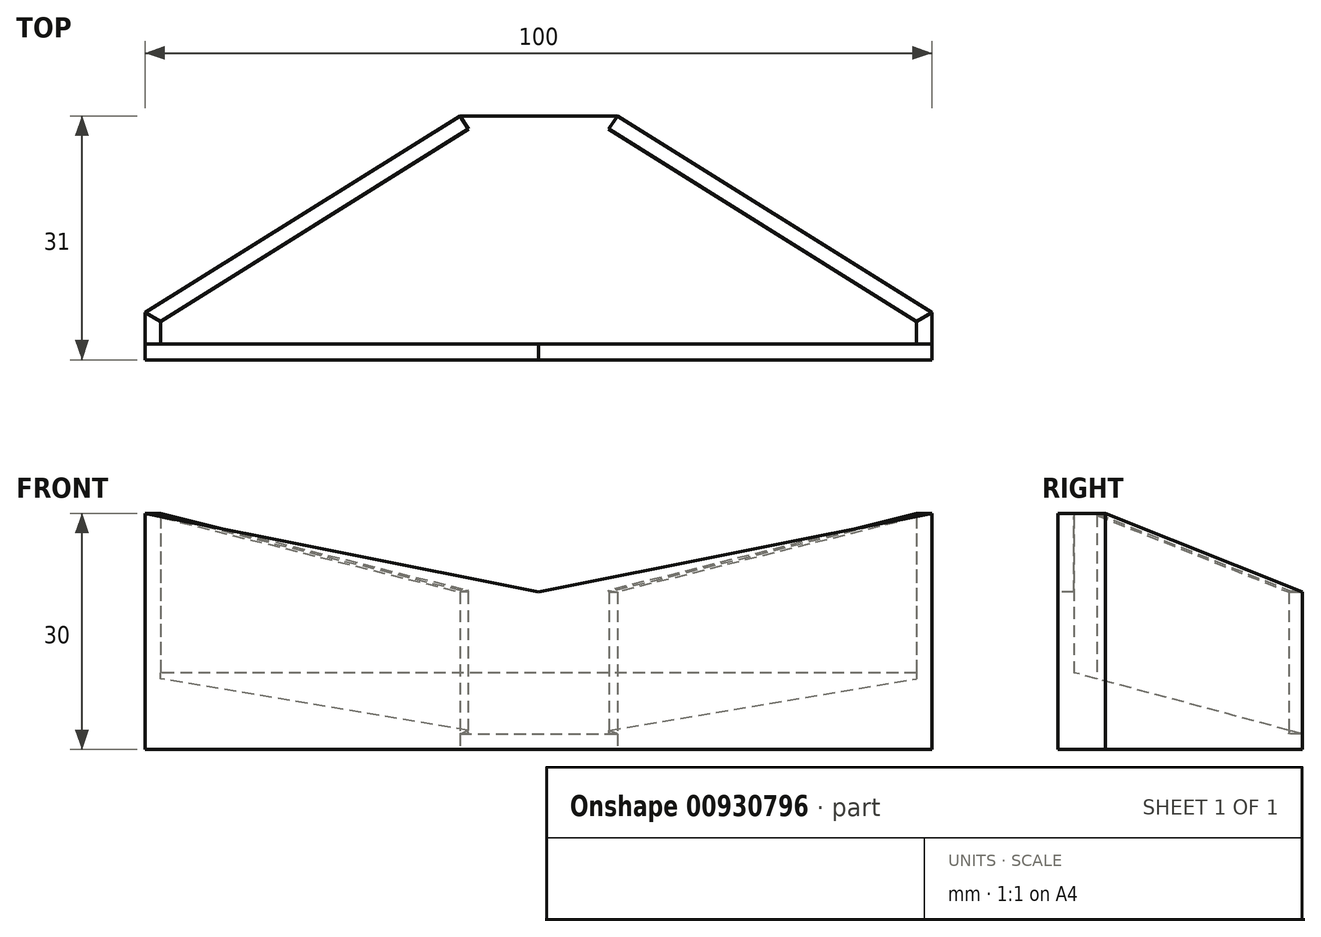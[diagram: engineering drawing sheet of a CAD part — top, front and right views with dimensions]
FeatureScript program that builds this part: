
annotation { "Feature Type Name" : "Feature", "Feature Type Description" : "" }
export const myFeature = defineFeature(function(context is Context, id is Id, definition is map)
    precondition{}
    {
        {
            var Q0;
            Q0=qCreatedBy(makeId("Top.planeOp"),FACE);
            var sketch = newSketch(context, id + "F0", { "sketchPlane" : qUnion([Q0])});
            skLineSegment(sketch, "E0", {"start": v(0, 0) * mm, "end": v(-50, 0) * mm});
            skLineSegment(sketch, "E1", {"start": v(-50, 0) * mm, "end": v(-50, 6) * mm});
            skLineSegment(sketch, "E2", {"start": v(-50, 6) * mm, "end": v(-10, 31) * mm});
            skLineSegment(sketch, "E3", {"start": v(-10, 31) * mm, "end": v(0, 31) * mm});
            skLineSegment(sketch, "E4.MirrorCS", {"start": v(50, 6) * mm, "end": v(10, 31) * mm});
            skLineSegment(sketch, "E5.MirrorCS", {"start": v(50, 0) * mm, "end": v(50, 6) * mm});
            skLineSegment(sketch, "E6.MirrorCS", {"start": v(10, 31) * mm, "end": v(0, 31) * mm});
            skLineSegment(sketch, "E7.MirrorCS", {"start": v(0, 0) * mm, "end": v(50, 0) * mm});
            skLineSegment(sketch, "E8.0", {"start": v(-48, 2) * mm, "end": v(-48, 4.9) * mm});
            skLineSegment(sketch, "E8.1", {"start": v(0, 2) * mm, "end": v(-48, 2) * mm});
            skLineSegment(sketch, "E8.2", {"start": v(-48, 4.9) * mm, "end": v(-9.43, 29) * mm});
            skLineSegment(sketch, "E8.3", {"start": v(0, 2) * mm, "end": v(48, 2) * mm});
            skLineSegment(sketch, "E8.6", {"start": v(48, 4.9) * mm, "end": v(9.43, 29) * mm});
            skLineSegment(sketch, "E8.7", {"start": v(48, 2) * mm, "end": v(48, 4.9) * mm});
            skLineSegment(sketch, "E9", {"start": v(-10, 31) * mm, "end": v(-9.43, 29) * mm});
            skLineSegment(sketch, "E10", {"start": v(10, 31) * mm, "end": v(9.43, 29) * mm});
            skLineSegment(sketch, "E11", {"start": v(-50, 6) * mm, "end": v(-48, 4.9) * mm});
            skLineSegment(sketch, "E12", {"start": v(48, 4.9) * mm, "end": v(50, 6) * mm});
            skSolve(sketch);
        }
        {
            var Q0;
            Q0=makeQuery(id+"F0.imprint","IMPRINT",FACE,{"disambiguationData":[TD([[makeQuery(id+"F0.imprint","IMPRINT",EDGE,{"derivedFrom":sQuery(id+"F0.wireOp",EDGE,"E0")}),-1.0]])]});
            var Q1;
            Q1 = qSketchRegion(id + "F4", true);
            extrude(context, id + "F1", {"entities" : qUnion([Q0, Q1]), "depth" : 30 * mm, "offsetDistance" : 25 * mm});
        }
        {
            var Q0;
            Q0=makeQuery(id+"F0.imprint","IMPRINT",FACE,{"disambiguationData":[TD([[makeQuery(id+"F0.imprint","IMPRINT",EDGE,{"derivedFrom":sQuery(id+"F0.wireOp",EDGE,"E3")}),-1.0]])]});
            extrude(context, id + "F2", {"entities" : qUnion([Q0]), "operationType" : NewBodyOperationType.ADD, "depth" : 2 * mm, "offsetDistance" : 25 * mm});
        }
        {
            var Q0;
            Q0=makeQuery(id+"F0.imprint","IMPRINT",FACE,{"disambiguationData":[TD([[makeQuery(id+"F0.imprint","IMPRINT",EDGE,{"derivedFrom":sQuery(id+"F0.wireOp",EDGE,"E2")}),-1.0]])]});
            var Q1;
            Q1=makeQuery(id+"F0.imprint","IMPRINT",FACE,{"disambiguationData":[TD([[makeQuery(id+"F0.imprint","IMPRINT",EDGE,{"derivedFrom":sQuery(id+"F0.wireOp",EDGE,"E4.MirrorCS")}),1.0]])]});
            extrude(context, id + "F3", {"entities" : qUnion([Q0, Q1]), "operationType" : NewBodyOperationType.ADD, "depth" : 20 * mm, "offsetDistance" : 25 * mm});
        }
        {
            var Q0;
            Q0=makeQuery(id+"F3.opExtrude","SWEPT_FACE",FACE,{"disambiguationData":[OSD([sQuery(id+"F0.wireOp",EDGE,"E2")])]});
            var sketch = newSketch(context, id + "F4", { "sketchPlane" : qUnion([Q0])});
            skLineSegment(sketch, "E13", {"start": v(-7.95, 20) * mm, "end": v(39.22, 20) * mm});
            skLineSegment(sketch, "E14", {"start": v(39.22, 20) * mm, "end": v(39.22, 30) * mm});
            skLineSegment(sketch, "E15", {"start": v(39.22, 30) * mm, "end": v(-7.95, 20) * mm});
            skSolve(sketch);
        }
        {
            var Q0;
            Q0=makeQuery(id+"F4.imprint","IMPRINT",FACE,{"disambiguationData":[TD([[makeQuery(id+"F4.imprint","IMPRINT",EDGE,{"derivedFrom":sQuery(id+"F4.wireOp",EDGE,"E13")}),-1.0]])]});
            extrude(context, id + "F5", {"entities" : qUnion([Q0]), "operationType" : NewBodyOperationType.ADD, "oppositeDirection" : true, "depth" : 2 * mm, "offsetDistance" : 25 * mm});
        }
        {
            var Q0;
            Q0=makeQuery(id+"F3.opExtrude","SWEPT_FACE",FACE,{"disambiguationData":[OSD([sQuery(id+"F0.wireOp",EDGE,"E4.MirrorCS")])]});
            var sketch = newSketch(context, id + "F6", { "sketchPlane" : qUnion([Q0])});
            skLineSegment(sketch, "E16", {"start": v(7.95, 20) * mm, "end": v(-39.22, 20) * mm});
            skLineSegment(sketch, "E17", {"start": v(-39.22, 20) * mm, "end": v(-39.22, 30) * mm});
            skLineSegment(sketch, "E18", {"start": v(-39.22, 30) * mm, "end": v(7.95, 20) * mm});
            skSolve(sketch);
        }
        {
            var Q0;
            Q0=makeQuery(id+"F6.imprint","IMPRINT",FACE,{"disambiguationData":[TD([[makeQuery(id+"F6.imprint","IMPRINT",EDGE,{"derivedFrom":sQuery(id+"F6.wireOp",EDGE,"E16")}),1.0]])]});
            extrude(context, id + "F7", {"entities" : qUnion([Q0]), "operationType" : NewBodyOperationType.ADD, "oppositeDirection" : true, "depth" : 2 * mm, "offsetDistance" : 25 * mm});
        }
        {
            var Q0;
            Q0=makeQuery(id+"F5.opExtrude","SWEPT_EDGE",EDGE,{"disambiguationData":[OSD([sQuery(id+"F0.wireOp",EDGE,"E2"),sQuery(id+"F0.wireOp",EDGE,"E3"),sQuery(id+"F0.wireOp",EDGE,"E9"),sQuery(id+"F4.wireOp",EDGE,"E13"),sQuery(id+"F4.wireOp",EDGE,"E15")])]});
            var Q1;
            Q1=makeQuery(id+"F3.boolean.opBoolean","SPLIT",EDGE,{"derivedFrom":makeQuery(id+"F3.opExtrude","SWEPT_EDGE",EDGE,{"disambiguationData":[OSD([sQuery(id+"F0.wireOp",EDGE,"E2"),sQuery(id+"F0.wireOp",EDGE,"E3"),sQuery(id+"F0.wireOp",EDGE,"E9")])]})});
            cPlane(context, id + "F8", {"entities" : qUnion([Q0, Q1]), "cplaneType" : CPlaneType.LINE_ANGLE, "offset" : 25 * mm, "angle" : 0 * degree, "width" : 150 * mm, "height" : 150 * mm});
        }
        {
            var Q0;
            Q0=qCreatedBy(id+"F8.planeOp",FACE);
            var sketch = newSketch(context, id + "F9", { "sketchPlane" : qUnion([Q0])});
            skLineSegment(sketch, "E19.bottom", {"start": v(-29.59, 20) * mm, "end": v(-31.59, 20) * mm});
            skLineSegment(sketch, "E19.top", {"start": v(-29.59, 2) * mm, "end": v(-31.59, 2) * mm});
            skLineSegment(sketch, "E19.left", {"start": v(-29.59, 20) * mm, "end": v(-29.59, 2) * mm});
            skLineSegment(sketch, "E19.right", {"start": v(-31.59, 20) * mm, "end": v(-31.59, 2) * mm});
            skSolve(sketch);
        }
        {
            var Q0;
            Q0=makeQuery(id+"F9.imprint","IMPRINT",FACE,{"disambiguationData":[TD([[makeQuery(id+"F9.imprint","IMPRINT",EDGE,{"derivedFrom":sQuery(id+"F9.wireOp",EDGE,"E19.bottom")}),1.0]])]});
            extrude(context, id + "F10", {"entities" : qUnion([Q0]), "operationType" : NewBodyOperationType.ADD, "depth" : 1 * mm, "offsetDistance" : 25 * mm});
        }
        {
            var Q0;
            Q0=makeQuery(id+"F7.opExtrude","SWEPT_EDGE",EDGE,{"disambiguationData":[OSD([sQuery(id+"F0.wireOp",EDGE,"E4.MirrorCS"),sQuery(id+"F0.wireOp",EDGE,"E6.MirrorCS"),sQuery(id+"F0.wireOp",EDGE,"E10"),sQuery(id+"F6.wireOp",EDGE,"E16"),sQuery(id+"F6.wireOp",EDGE,"E18")])]});
            var Q1;
            Q1=makeQuery(id+"F3.boolean.opBoolean","SPLIT",EDGE,{"derivedFrom":makeQuery(id+"F3.opExtrude","SWEPT_EDGE",EDGE,{"disambiguationData":[OSD([sQuery(id+"F0.wireOp",EDGE,"E4.MirrorCS"),sQuery(id+"F0.wireOp",EDGE,"E6.MirrorCS"),sQuery(id+"F0.wireOp",EDGE,"E10")])]})});
            cPlane(context, id + "F11", {"entities" : qUnion([Q0, Q1]), "cplaneType" : CPlaneType.LINE_ANGLE, "offset" : 25 * mm, "angle" : 0 * degree, "width" : 150 * mm, "height" : 150 * mm});
        }
        {
            var Q0;
            Q0=qCreatedBy(id+"F11.planeOp",FACE);
            var sketch = newSketch(context, id + "F12", { "sketchPlane" : qUnion([Q0])});
            skLineSegment(sketch, "E20.bottom", {"start": v(-31.59, 20) * mm, "end": v(-29.59, 20) * mm});
            skLineSegment(sketch, "E20.top", {"start": v(-31.59, 2) * mm, "end": v(-29.59, 2) * mm});
            skLineSegment(sketch, "E20.left", {"start": v(-31.59, 20) * mm, "end": v(-31.59, 2) * mm});
            skLineSegment(sketch, "E20.right", {"start": v(-29.59, 20) * mm, "end": v(-29.59, 2) * mm});
            skSolve(sketch);
        }
        {
            var Q0;
            Q0=makeQuery(id+"F12.imprint","IMPRINT",FACE,{"disambiguationData":[TD([[makeQuery(id+"F12.imprint","IMPRINT",EDGE,{"derivedFrom":sQuery(id+"F12.wireOp",EDGE,"E20.bottom")}),-1.0]])]});
            extrude(context, id + "F13", {"entities" : qUnion([Q0]), "operationType" : NewBodyOperationType.ADD, "oppositeDirection" : true, "depth" : 1 * mm, "offsetDistance" : 25 * mm});
        }
        {
            var Q0;
            Q0=makeQuery(id+"F5.opExtrude","CAP_EDGE",EDGE,{"disambiguationData":[OSD([sQuery(id+"F4.wireOp",EDGE,"E15")])],"isStart":true});
            var Q1;
            Q1=makeQuery(id+"F1.opExtrude","CAP_EDGE",EDGE,{"disambiguationData":[OSD([sQuery(id+"F0.wireOp",EDGE,"E11")])],"isStart":false});
            cPlane(context, id + "F14", {"entities" : qUnion([Q0, Q1]), "cplaneType" : CPlaneType.LINE_ANGLE, "offset" : 25 * mm, "angle" : 0 * degree, "width" : 150 * mm, "height" : 150 * mm});
        }
        {
            var Q0;
            Q0=qCreatedBy(id+"F14.planeOp",FACE);
            var sketch = newSketch(context, id + "F15", { "sketchPlane" : qUnion([Q0])});
            skLineSegment(sketch, "E21", {"start": v(-51.18, 1.42) * mm, "end": v(-11.81, -24.52) * mm});
            skLineSegment(sketch, "E22", {"start": v(-11.81, -24.52) * mm, "end": v(-12.9, -26.17) * mm});
            skLineSegment(sketch, "E23", {"start": v(-12.9, -26.17) * mm, "end": v(-53.17, 0.35) * mm});
            skLineSegment(sketch, "E24", {"start": v(-53.17, 0.35) * mm, "end": v(-51.18, 1.42) * mm});
            skSolve(sketch);
        }
        {
            var Q0;
            Q0=makeQuery(id+"F15.imprint","IMPRINT",FACE,{"disambiguationData":[TD([[makeQuery(id+"F15.imprint","IMPRINT",EDGE,{"derivedFrom":sQuery(id+"F15.wireOp",EDGE,"E21")}),-1.0]])]});
            var Q1;
            Q1=makeQuery(id+"F5.opExtrude","SWEPT_FACE",FACE,{"disambiguationData":[OSD([sQuery(id+"F4.wireOp",EDGE,"E15")])]});
            extrude(context, id + "F16", {"entities" : qUnion([Q0]), "operationType" : NewBodyOperationType.ADD, "endBound" : BoundingType.UP_TO_SURFACE, "depth" : 25 * mm, "endBoundEntityFace" : qUnion([Q1]), "offsetDistance" : 25 * mm});
        }
        {
            var Q0;
            Q0=makeQuery(id+"F1.opExtrude","CAP_EDGE",EDGE,{"disambiguationData":[OSD([sQuery(id+"F0.wireOp",EDGE,"E12")])],"isStart":false});
            var Q1;
            Q1=makeQuery(id+"F7.opExtrude","CAP_EDGE",EDGE,{"disambiguationData":[OSD([sQuery(id+"F6.wireOp",EDGE,"E18")])],"isStart":true});
            cPlane(context, id + "F17", {"entities" : qUnion([Q0, Q1]), "cplaneType" : CPlaneType.LINE_ANGLE, "offset" : 25 * mm, "angle" : 0 * degree, "width" : 150 * mm, "height" : 150 * mm});
        }
        {
            var Q0;
            Q0=qCreatedBy(id+"F17.planeOp",FACE);
            var sketch = newSketch(context, id + "F18", { "sketchPlane" : qUnion([Q0])});
            skLineSegment(sketch, "E25", {"start": v(53.17, -0.35) * mm, "end": v(51.18, -1.42) * mm});
            skLineSegment(sketch, "E26", {"start": v(51.18, -1.42) * mm, "end": v(11.81, 24.52) * mm});
            skLineSegment(sketch, "E27", {"start": v(11.81, 24.52) * mm, "end": v(12.9, 26.17) * mm});
            skLineSegment(sketch, "E28", {"start": v(12.9, 26.17) * mm, "end": v(53.17, -0.35) * mm});
            skSolve(sketch);
        }
        {
            var Q0;
            Q0 = qSketchRegion(id + "F18", true);
            var Q1;
            Q1=makeQuery(id+"F7.opExtrude","SWEPT_FACE",FACE,{"disambiguationData":[OSD([sQuery(id+"F6.wireOp",EDGE,"E18")])]});
            extrude(context, id + "F19", {"entities" : qUnion([Q0]), "operationType" : NewBodyOperationType.ADD, "endBound" : BoundingType.UP_TO_SURFACE, "oppositeDirection" : true, "depth" : 25 * mm, "endBoundEntityFace" : qUnion([Q1]), "offsetDistance" : 25 * mm});
        }
        {
            var Q0;
            Q0=makeQuery(id+"F7.boolean.opBoolean","SPLIT",EDGE,{"derivedFrom":makeQuery(id+"F3.boolean.opBoolean","SPLIT",EDGE,{"derivedFrom":makeQuery(id+"F2.boolean.opBoolean","SPLIT",EDGE,{"derivedFrom":makeQuery(id+"F1.opExtrude","SWEPT_EDGE",EDGE,{"disambiguationData":[OSD([sQuery(id+"F0.wireOp",EDGE,"E8.6"),sQuery(id+"F0.wireOp",EDGE,"E8.7"),sQuery(id+"F0.wireOp",EDGE,"E12")])]})})})});
            var Q1;
            Q1=makeQuery(id+"F19.boolean.opBoolean","MERGE",EDGE,{"derivedFrom":[makeQuery(id+"F7.opExtrude","CAP_EDGE",EDGE,{"disambiguationData":[OSD([sQuery(id+"F6.wireOp",EDGE,"E18")])],"isStart":false}),makeQuery(id+"F19.opExtrude","CAP_EDGE",EDGE,{"disambiguationData":[OSD([sQuery(id+"F18.wireOp",EDGE,"E26")])],"isStart":false})]});
            cPlane(context, id + "F20", {"entities" : qUnion([Q0, Q1]), "cplaneType" : CPlaneType.LINE_ANGLE, "offset" : 25 * mm, "angle" : 0 * degree, "width" : 150 * mm, "height" : 150 * mm});
        }
        {
            var Q0;
            Q0=makeQuery(id+"F2.opExtrude","CAP_EDGE",EDGE,{"disambiguationData":[OSD([sQuery(id+"F0.wireOp",EDGE,"E3"),sQuery(id+"F0.wireOp",EDGE,"E6.MirrorCS")])],"isStart":false});
            var Q1;
            Q1=makeQuery(id+"F2.opExtrude","CAP_FACE",FACE,{"disambiguationData":[OSD([sQuery(id+"F0.wireOp",EDGE,"E3"),sQuery(id+"F0.wireOp",EDGE,"E6.MirrorCS"),sQuery(id+"F0.wireOp",EDGE,"E8.1"),sQuery(id+"F0.wireOp",EDGE,"E8.2"),sQuery(id+"F0.wireOp",EDGE,"E8.3"),sQuery(id+"F0.wireOp",EDGE,"E8.6"),sQuery(id+"F0.wireOp",EDGE,"E8.7"),sQuery(id+"F0.wireOp",EDGE,"E9"),sQuery(id+"F0.wireOp",EDGE,"E10"),sQuery(id+"F0.wireOp",EDGE,"E8.0")])],"isStart":false});
            cPlane(context, id + "F21", {"entities" : qUnion([Q0, Q1]), "cplaneType" : CPlaneType.LINE_ANGLE, "offset" : 25 * mm, "angle" : 15 * degree, "oppositeDirection" : true, "width" : 150 * mm, "height" : 150 * mm});
        }
        {
            var Q0;
            Q0=makeQuery(id+"F1.opExtrude","SWEPT_FACE",FACE,{"disambiguationData":[OSD([sQuery(id+"F0.wireOp",EDGE,"E8.1"),sQuery(id+"F0.wireOp",EDGE,"E8.3")])]});
            var sketch = newSketch(context, id + "F22", { "sketchPlane" : qUnion([Q0])});
            skLineSegment(sketch, "E29", {"start": v(-48, 12) * mm, "end": v(48, 12) * mm});
            skLineSegment(sketch, "E30", {"start": v(-48, 12) * mm, "end": v(-48, 2) * mm, "construction": true});
            skSolve(sketch);
        }
        {
            var Q0;
            Q0=qCreatedBy(id+"F21.planeOp",FACE);
            var sketch = newSketch(context, id + "F23", { "sketchPlane" : qUnion([Q0])});
            skLineSegment(sketch, "E31", {"start": v(6.23, -29.42) * mm, "end": v(-6.23, -29.42) * mm});
            skLineSegment(sketch, "E32", {"start": v(-6.23, -29.42) * mm, "end": v(-48, -4.2) * mm});
            skLineSegment(sketch, "E33", {"start": v(-48, -4.2) * mm, "end": v(-48, 1.17) * mm});
            skLineSegment(sketch, "E34", {"start": v(48, 1.17) * mm, "end": v(48, -4.2) * mm});
            skLineSegment(sketch, "E35", {"start": v(48, -4.2) * mm, "end": v(6.23, -29.42) * mm});
            skLineSegment(sketch, "E36", {"start": v(10, -29.42) * mm, "end": v(8.94, -27.78) * mm});
            skLineSegment(sketch, "E37", {"start": v(-8.94, -27.79) * mm, "end": v(-6.23, -29.42) * mm});
            skLineSegment(sketch, "E38", {"start": v(-8.94, -27.78) * mm, "end": v(-6.23, -29.42) * mm});
            skLineSegment(sketch, "E39", {"start": v(-6.23, -29.42) * mm, "end": v(-10, -29.42) * mm});
            skLineSegment(sketch, "E40", {"start": v(-10, -29.42) * mm, "end": v(-8.94, -27.78) * mm});
            skLineSegment(sketch, "E41", {"start": v(8.94, -27.78) * mm, "end": v(10, -29.42) * mm});
            skLineSegment(sketch, "E42", {"start": v(10, -29.42) * mm, "end": v(6.23, -29.42) * mm});
            skLineSegment(sketch, "E43", {"start": v(6.23, -29.42) * mm, "end": v(8.94, -27.78) * mm});
            skLineSegment(sketch, "E44", {"start": v(-48, 1.17) * mm, "end": v(48, 1.17) * mm});
            skSolve(sketch);
        }
        {
            var Q0;
            {var subQ3=sQuery(id+"F23.wireOp",EDGE,"E31");Q0=makeQuery(id+"F23.imprint","IMPRINT",FACE,{"disambiguationData":[TD([[makeQuery(id+"F23.imprint","IMPRINT",EDGE,{"derivedFrom":subQ3}),-1.0]])]});}
            var Q1;
            {var subQ0=sQuery(id+"F23.wireOp",EDGE,"E39");Q1=makeQuery(id+"F23.imprint","IMPRINT",FACE,{"disambiguationData":[TD([[makeQuery(id+"F23.imprint","IMPRINT",EDGE,{"derivedFrom":subQ0}),-1.0]])]});}
            var Q2;
            {var subQ2=sQuery(id+"F23.wireOp",EDGE,"E36");Q2=makeQuery(id+"F23.imprint","IMPRINT",FACE,{"disambiguationData":[TD([[makeQuery(id+"F23.imprint","IMPRINT",EDGE,{"derivedFrom":subQ2}),1.0]])]});}
            var Q3;
            Q3=makeQuery(id+"F1.opExtrude","SWEPT_BODY",BODY,{"disambiguationData":[OSD([sQuery(id+"F0.wireOp",EDGE,"E0"),sQuery(id+"F0.wireOp",EDGE,"E1"),sQuery(id+"F0.wireOp",EDGE,"E5.MirrorCS"),sQuery(id+"F0.wireOp",EDGE,"E7.MirrorCS"),sQuery(id+"F0.wireOp",EDGE,"E8.1"),sQuery(id+"F0.wireOp",EDGE,"E8.3"),sQuery(id+"F0.wireOp",EDGE,"E8.7"),sQuery(id+"F0.wireOp",EDGE,"E8.0"),sQuery(id+"F0.wireOp",EDGE,"E11"),sQuery(id+"F0.wireOp",EDGE,"E12")])]});
            extrude(context, id + "F24", {"entities" : qUnion([Q0, Q1, Q2]), "operationType" : NewBodyOperationType.ADD, "endBound" : BoundingType.UP_TO_BODY, "depth" : 25 * mm, "endBoundEntityBody" : qUnion([Q3]), "offsetDistance" : 25 * mm});
        }
        {
            var Q0;
            Q0=makeQuery(id+"F1.opExtrude","SWEPT_FACE",FACE,{"disambiguationData":[OSD([sQuery(id+"F0.wireOp",EDGE,"E0"),sQuery(id+"F0.wireOp",EDGE,"E7.MirrorCS")])]});
            var sketch = newSketch(context, id + "F25", { "sketchPlane" : qUnion([Q0])});
            skLineSegment(sketch, "E45", {"start": v(0, 0) * mm, "end": v(0, 20) * mm});
            skLineSegment(sketch, "E46", {"start": v(0, 20) * mm, "end": v(-50, 30) * mm});
            skLineSegment(sketch, "E47", {"start": v(0, 20) * mm, "end": v(50, 30) * mm});
            skLineSegment(sketch, "E48", {"start": v(50, 30) * mm, "end": v(50, 0) * mm});
            skLineSegment(sketch, "E49", {"start": v(50, 0) * mm, "end": v(-50, 0) * mm});
            skLineSegment(sketch, "E50", {"start": v(-50, 0) * mm, "end": v(-50, 30) * mm});
            skSolve(sketch);
        }
        {
            var Q0;
            Q0=makeQuery(id+"F25.imprint","IMPRINT",FACE,{"disambiguationData":[TD([[makeQuery(id+"F25.imprint","IMPRINT",EDGE,{"derivedFrom":sQuery(id+"F25.wireOp",EDGE,"E46")}),-1.0]])]});
            extrude(context, id + "F26", {"entities" : qUnion([Q0]), "operationType" : NewBodyOperationType.REMOVE, "oppositeDirection" : true, "depth" : 2 * mm, "offsetDistance" : 25 * mm});
        }
    });
